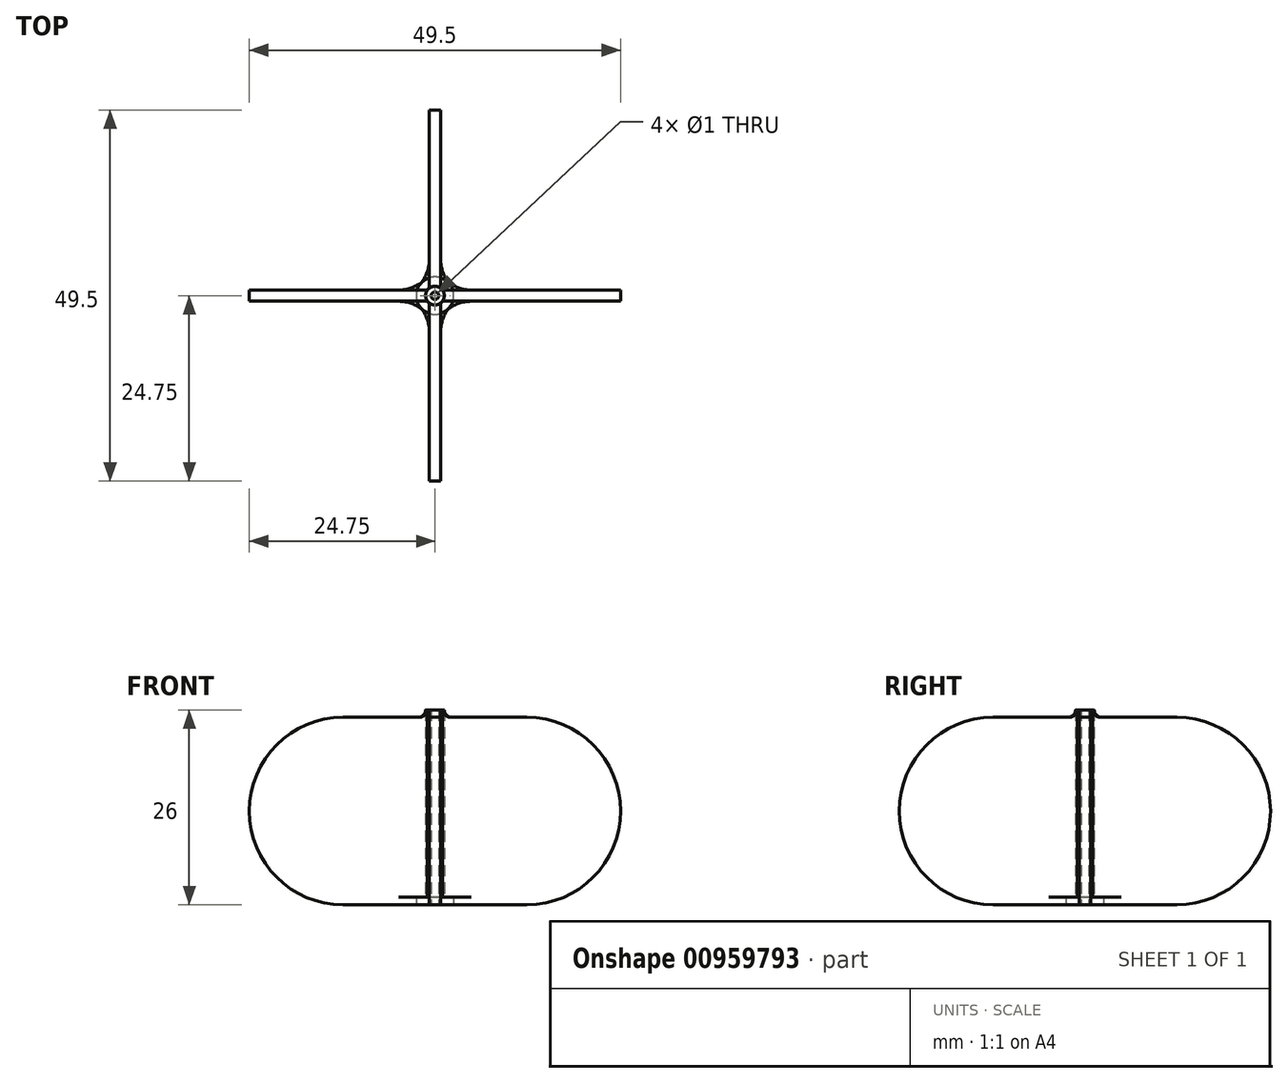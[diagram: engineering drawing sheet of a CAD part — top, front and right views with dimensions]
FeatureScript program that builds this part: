
annotation { "Feature Type Name" : "Feature", "Feature Type Description" : "" }
export const myFeature = defineFeature(function(context is Context, id is Id, definition is map)
    precondition{}
    {
        {
            var Q0;
            Q0=qCreatedBy(makeId("Top.planeOp"),FACE);
            var sketch = newSketch(context, id + "F0", { "sketchPlane" : qUnion([Q0])});
            skCircle(sketch, "E0", {"center": v(0, 0) * mm, "radius": 2.5 * mm});
            skCircle(sketch, "E1", {"center": v(0, 0) * mm, "radius": 0.5 * mm});
            skSolve(sketch);
        }
        {
            var Q0;
            Q0 = qSketchRegion(id + "F0", true);
            extrude(context, id + "F1", {"entities" : qUnion([Q0]), "depth" : (1) * mm, "offsetDistance" : 25 * mm});
        }
        {
            var Q0;
            Q0=makeQuery(id+"F1.opExtrude","CAP_FACE",FACE,{"disambiguationData":[OSD([sQuery(id+"F0.wireOp",EDGE,"E0"),sQuery(id+"F0.wireOp",EDGE,"E1")])],"isStart":false});
            var sketch = newSketch(context, id + "F2", { "sketchPlane" : qUnion([Q0])});
            skCircle(sketch, "E2", {"center": v(0, 0) * mm, "radius": 0.5 * mm});
            skCircle(sketch, "E3", {"center": v(0, 0) * mm, "radius": 1.25 * mm});
            skSolve(sketch);
        }
        {
            var Q0;
            Q0 = qSketchRegion(id + "F2", true);
            extrude(context, id + "F3", {"entities" : qUnion([Q0]), "operationType" : NewBodyOperationType.ADD, "depth" : 25 * mm, "offsetDistance" : 25 * mm});
        }
        {
            var Q0;
            Q0=qCreatedBy(makeId("Front.planeOp"),FACE);
            var sketch = newSketch(context, id + "F4", { "sketchPlane" : qUnion([Q0])});
            skLineSegment(sketch, "E4.bottom", {"start": v(1, 0) * mm, "end": v(12.25, 0) * mm});
            skLineSegment(sketch, "E4.top", {"start": v(1, 25) * mm, "end": v(12.25, 25) * mm});
            skLineSegment(sketch, "E4.left", {"start": v(1, 0) * mm, "end": v(1, 25) * mm});
            skArc(sketch, "E5", {"start": v(12.25, 25) * mm, "mid": v(24.75, 12.5) * mm, "end": v(12.25, 0) * mm});
            skSolve(sketch);
        }
        {
            var Q0;
            Q0=makeQuery(id+"F4.imprint","IMPRINT",FACE,{"disambiguationData":[TD([[makeQuery(id+"F4.imprint","IMPRINT",EDGE,{"derivedFrom":sQuery(id+"F4.wireOp",EDGE,"E4.bottom")}),1.0]])]});
            extrude(context, id + "F5", {"entities" : qUnion([Q0]), "operationType" : NewBodyOperationType.ADD, "depth" : .75 * mm, "offsetDistance" : 25 * mm, "hasSecondDirection" : true, "secondDirectionOppositeDirection" : true, "secondDirectionDepth" : .75 * mm});
        }
        {
            var Q0;
            Q0=makeQuery(id+"F1.opExtrude","SWEPT_BODY",BODY,{"disambiguationData":[OSD([sQuery(id+"F0.wireOp",EDGE,"E0"),sQuery(id+"F0.wireOp",EDGE,"E1")])]});
            var Q1;
            Q1=makeQuery(id+"F3.boolean.opBoolean","MERGE",FACE,{"derivedFrom":[makeQuery(id+"F1.opExtrude","SWEPT_FACE",FACE,{"disambiguationData":[OSD([sQuery(id+"F0.wireOp",EDGE,"E1")])]}),makeQuery(id+"F3.opExtrude","SWEPT_FACE",FACE,{"disambiguationData":[OSD([sQuery(id+"F2.wireOp",EDGE,"E2")])]})]});
            circularPattern(context, id + "F6", {"entities" : qUnion([Q0]), "axis" : qUnion([Q1]), "angle" : 360 * degree, "instanceCount" : 4, "equalSpace" : true});
        }
        {
            var Q0;
            Q0=makeQuery(id+"F6.opPattern","COPY",EDGE,{"derivedFrom":makeQuery(id+"F5.opExtrude","CAP_EDGE",EDGE,{"disambiguationData":[OSD([sQuery(id+"F4.wireOp",EDGE,"E4.left")])],"isStart":true}),"instanceName":"2"});
            var Q1;
            Q1=makeQuery(id+"F6.opPattern","COPY",EDGE,{"derivedFrom":makeQuery(id+"F5.opExtrude","CAP_EDGE",EDGE,{"disambiguationData":[OSD([sQuery(id+"F4.wireOp",EDGE,"E4.left")])],"isStart":false}),"instanceName":"3"});
            var Q2;
            Q2=makeQuery(id+"F6.opPattern","COPY",EDGE,{"derivedFrom":makeQuery(id+"F5.opExtrude","CAP_EDGE",EDGE,{"disambiguationData":[OSD([sQuery(id+"F4.wireOp",EDGE,"E4.left")])],"isStart":false}),"instanceName":"2"});
            var Q3;
            Q3=makeQuery(id+"F6.opPattern","COPY",EDGE,{"derivedFrom":makeQuery(id+"F5.opExtrude","CAP_EDGE",EDGE,{"disambiguationData":[OSD([sQuery(id+"F4.wireOp",EDGE,"E4.left")])],"isStart":true}),"instanceName":"1"});
            var Q4;
            Q4=makeQuery(id+"F6.opPattern","COPY",EDGE,{"derivedFrom":makeQuery(id+"F5.boolean.opBoolean","INTERSECT",EDGE,{"derivedFrom":[makeQuery(id+"F3.opExtrude","SWEPT_FACE",FACE,{"disambiguationData":[OSD([sQuery(id+"F2.wireOp",EDGE,"E3")])]}),makeQuery(id+"F5.opExtrude","SWEPT_FACE",FACE,{"disambiguationData":[OSD([sQuery(id+"F4.wireOp",EDGE,"E4.top")])]})]}),"instanceName":"2"});
            var Q5;
            Q5=makeQuery(id+"F6.opPattern","COPY",EDGE,{"derivedFrom":makeQuery(id+"F5.boolean.opBoolean","INTERSECT",EDGE,{"derivedFrom":[makeQuery(id+"F3.opExtrude","SWEPT_FACE",FACE,{"disambiguationData":[OSD([sQuery(id+"F2.wireOp",EDGE,"E3")])]}),makeQuery(id+"F5.opExtrude","SWEPT_FACE",FACE,{"disambiguationData":[OSD([sQuery(id+"F4.wireOp",EDGE,"E4.top")])]})]}),"instanceName":"1"});
            var Q6;
            Q6=makeQuery(id+"F6.opPattern","COPY",EDGE,{"derivedFrom":makeQuery(id+"F5.boolean.opBoolean","INTERSECT",EDGE,{"derivedFrom":[makeQuery(id+"F3.opExtrude","SWEPT_FACE",FACE,{"disambiguationData":[OSD([sQuery(id+"F2.wireOp",EDGE,"E3")])]}),makeQuery(id+"F5.opExtrude","SWEPT_FACE",FACE,{"disambiguationData":[OSD([sQuery(id+"F4.wireOp",EDGE,"E4.top")])]})]}),"instanceName":"3"});
            var Q7;
            Q7=makeQuery(id+"F6.opPattern","COPY",EDGE,{"derivedFrom":makeQuery(id+"F5.opExtrude","CAP_EDGE",EDGE,{"disambiguationData":[OSD([sQuery(id+"F4.wireOp",EDGE,"E4.left")])],"isStart":true}),"instanceName":"3"});
            var Q8;
            Q8=makeQuery(id+"F5.opExtrude","CAP_EDGE",EDGE,{"disambiguationData":[OSD([sQuery(id+"F4.wireOp",EDGE,"E4.left")])],"isStart":false});
            var Q9;
            Q9=makeQuery(id+"F5.boolean.opBoolean","INTERSECT",EDGE,{"derivedFrom":[makeQuery(id+"F3.opExtrude","SWEPT_FACE",FACE,{"disambiguationData":[OSD([sQuery(id+"F2.wireOp",EDGE,"E3")])]}),makeQuery(id+"F5.opExtrude","SWEPT_FACE",FACE,{"disambiguationData":[OSD([sQuery(id+"F4.wireOp",EDGE,"E4.top")])]})]});
            var Q10;
            Q10=makeQuery(id+"F5.opExtrude","CAP_EDGE",EDGE,{"disambiguationData":[OSD([sQuery(id+"F4.wireOp",EDGE,"E4.left")])],"isStart":true});
            var Q11;
            Q11=makeQuery(id+"F6.opPattern","COPY",EDGE,{"derivedFrom":makeQuery(id+"F5.opExtrude","CAP_EDGE",EDGE,{"disambiguationData":[OSD([sQuery(id+"F4.wireOp",EDGE,"E4.left")])],"isStart":false}),"instanceName":"1"});
            fillet(context, id + "F7", {"entities" : qUnion([Q0, Q1, Q2, Q3, Q4, Q5, Q6, Q7, Q8, Q9, Q10, Q11]), "radius" : 1 * mm, "tangentPropagation" : true, "allowEdgeOverflow" : false});
        }
        {
            var Q0;
            Q0=makeQuery(id+"F6.opPattern","COPY",EDGE,{"derivedFrom":makeQuery(id+"F5.boolean.opBoolean","INTERSECT",EDGE,{"derivedFrom":[makeQuery(id+"F1.opExtrude","SWEPT_FACE",FACE,{"disambiguationData":[OSD([sQuery(id+"F0.wireOp",EDGE,"E0")])]}),makeQuery(id+"F5.opExtrude","CAP_FACE",FACE,{"disambiguationData":[OSD([sQuery(id+"F4.wireOp",EDGE,"E4.bottom"),sQuery(id+"F4.wireOp",EDGE,"E4.top"),sQuery(id+"F4.wireOp",EDGE,"E4.left"),sQuery(id+"F4.wireOp",EDGE,"E5")])],"isStart":false})]}),"instanceName":"1"});
            var Q1;
            Q1=makeQuery(id+"F5.boolean.opBoolean","INTERSECT",EDGE,{"derivedFrom":[makeQuery(id+"F1.opExtrude","SWEPT_FACE",FACE,{"disambiguationData":[OSD([sQuery(id+"F0.wireOp",EDGE,"E0")])]}),makeQuery(id+"F5.opExtrude","CAP_FACE",FACE,{"disambiguationData":[OSD([sQuery(id+"F4.wireOp",EDGE,"E4.bottom"),sQuery(id+"F4.wireOp",EDGE,"E4.top"),sQuery(id+"F4.wireOp",EDGE,"E4.left"),sQuery(id+"F4.wireOp",EDGE,"E5")])],"isStart":true})]});
            var Q2;
            Q2=makeQuery(id+"F6.opPattern","COPY",EDGE,{"derivedFrom":makeQuery(id+"F5.boolean.opBoolean","INTERSECT",EDGE,{"derivedFrom":[makeQuery(id+"F1.opExtrude","SWEPT_FACE",FACE,{"disambiguationData":[OSD([sQuery(id+"F0.wireOp",EDGE,"E0")])]}),makeQuery(id+"F5.opExtrude","CAP_FACE",FACE,{"disambiguationData":[OSD([sQuery(id+"F4.wireOp",EDGE,"E4.bottom"),sQuery(id+"F4.wireOp",EDGE,"E4.top"),sQuery(id+"F4.wireOp",EDGE,"E4.left"),sQuery(id+"F4.wireOp",EDGE,"E5")])],"isStart":true})]}),"instanceName":"1"});
            var Q3;
            Q3=makeQuery(id+"F6.opPattern","COPY",EDGE,{"derivedFrom":makeQuery(id+"F5.boolean.opBoolean","INTERSECT",EDGE,{"derivedFrom":[makeQuery(id+"F1.opExtrude","SWEPT_FACE",FACE,{"disambiguationData":[OSD([sQuery(id+"F0.wireOp",EDGE,"E0")])]}),makeQuery(id+"F5.opExtrude","CAP_FACE",FACE,{"disambiguationData":[OSD([sQuery(id+"F4.wireOp",EDGE,"E4.bottom"),sQuery(id+"F4.wireOp",EDGE,"E4.top"),sQuery(id+"F4.wireOp",EDGE,"E4.left"),sQuery(id+"F4.wireOp",EDGE,"E5")])],"isStart":false})]}),"instanceName":"2"});
            var Q4;
            Q4=makeQuery(id+"F6.opPattern","COPY",EDGE,{"derivedFrom":makeQuery(id+"F5.boolean.opBoolean","INTERSECT",EDGE,{"derivedFrom":[makeQuery(id+"F1.opExtrude","SWEPT_FACE",FACE,{"disambiguationData":[OSD([sQuery(id+"F0.wireOp",EDGE,"E0")])]}),makeQuery(id+"F5.opExtrude","CAP_FACE",FACE,{"disambiguationData":[OSD([sQuery(id+"F4.wireOp",EDGE,"E4.bottom"),sQuery(id+"F4.wireOp",EDGE,"E4.top"),sQuery(id+"F4.wireOp",EDGE,"E4.left"),sQuery(id+"F4.wireOp",EDGE,"E5")])],"isStart":true})]}),"instanceName":"2"});
            var Q5;
            Q5=makeQuery(id+"F6.opPattern","COPY",EDGE,{"derivedFrom":makeQuery(id+"F5.boolean.opBoolean","INTERSECT",EDGE,{"derivedFrom":[makeQuery(id+"F1.opExtrude","SWEPT_FACE",FACE,{"disambiguationData":[OSD([sQuery(id+"F0.wireOp",EDGE,"E0")])]}),makeQuery(id+"F5.opExtrude","CAP_FACE",FACE,{"disambiguationData":[OSD([sQuery(id+"F4.wireOp",EDGE,"E4.bottom"),sQuery(id+"F4.wireOp",EDGE,"E4.top"),sQuery(id+"F4.wireOp",EDGE,"E4.left"),sQuery(id+"F4.wireOp",EDGE,"E5")])],"isStart":false})]}),"instanceName":"3"});
            var Q6;
            Q6=makeQuery(id+"F6.opPattern","COPY",EDGE,{"derivedFrom":makeQuery(id+"F5.boolean.opBoolean","INTERSECT",EDGE,{"derivedFrom":[makeQuery(id+"F1.opExtrude","SWEPT_FACE",FACE,{"disambiguationData":[OSD([sQuery(id+"F0.wireOp",EDGE,"E0")])]}),makeQuery(id+"F5.opExtrude","CAP_FACE",FACE,{"disambiguationData":[OSD([sQuery(id+"F4.wireOp",EDGE,"E4.bottom"),sQuery(id+"F4.wireOp",EDGE,"E4.top"),sQuery(id+"F4.wireOp",EDGE,"E4.left"),sQuery(id+"F4.wireOp",EDGE,"E5")])],"isStart":true})]}),"instanceName":"3"});
            var Q7;
            Q7=makeQuery(id+"F5.boolean.opBoolean","INTERSECT",EDGE,{"derivedFrom":[makeQuery(id+"F1.opExtrude","SWEPT_FACE",FACE,{"disambiguationData":[OSD([sQuery(id+"F0.wireOp",EDGE,"E0")])]}),makeQuery(id+"F5.opExtrude","CAP_FACE",FACE,{"disambiguationData":[OSD([sQuery(id+"F4.wireOp",EDGE,"E4.bottom"),sQuery(id+"F4.wireOp",EDGE,"E4.top"),sQuery(id+"F4.wireOp",EDGE,"E4.left"),sQuery(id+"F4.wireOp",EDGE,"E5")])],"isStart":false})]});
            fillet(context, id + "F8", {"entities" : qUnion([Q0, Q1, Q2, Q3, Q4, Q5, Q6, Q7]), "radius" : 5 * mm, "tangentPropagation" : true, "allowEdgeOverflow" : false});
        }
    });
